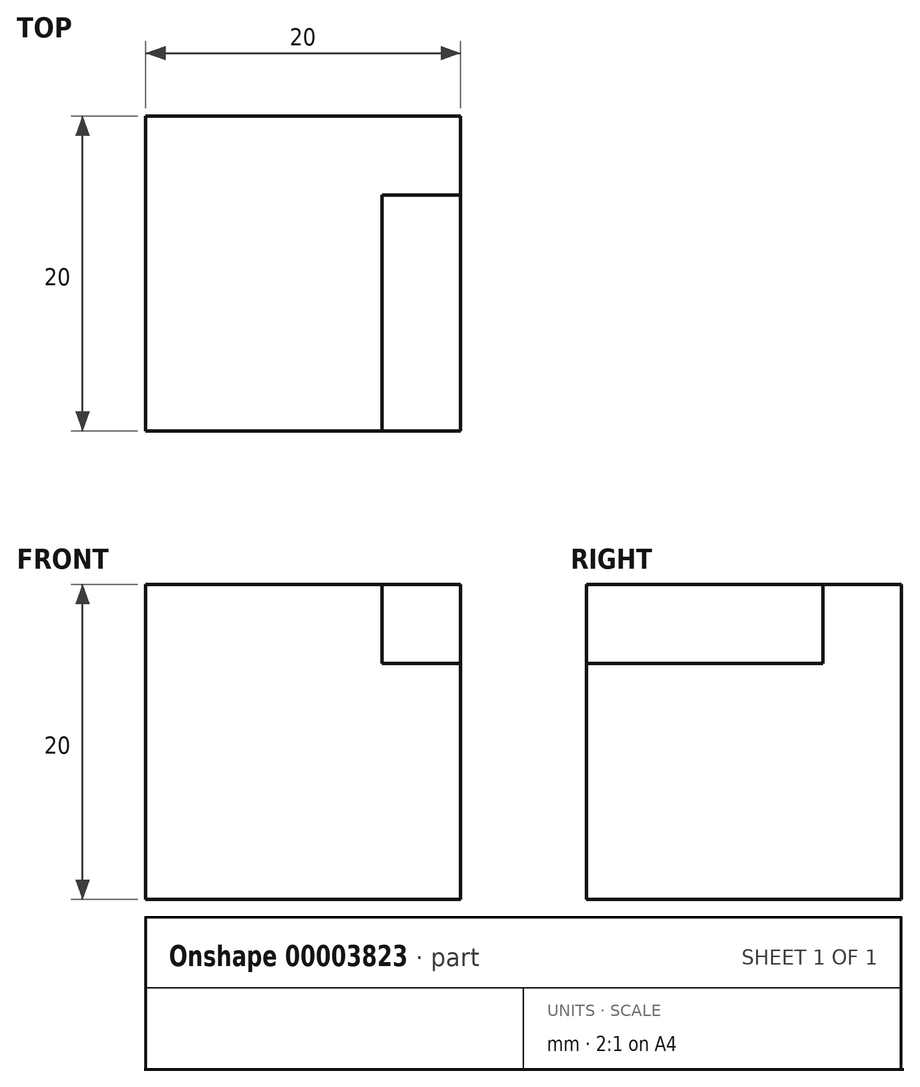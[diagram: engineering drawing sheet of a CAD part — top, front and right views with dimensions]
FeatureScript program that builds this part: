
annotation { "Feature Type Name" : "Feature", "Feature Type Description" : "" }
export const myFeature = defineFeature(function(context is Context, id is Id, definition is map)
    precondition{}
    {
        {
            var Q0;
            Q0=qCreatedBy(makeId("Front.planeOp"),FACE);
            var sketch = newSketch(context, id + "F0", { "sketchPlane" : qUnion([Q0])});
            skLineSegment(sketch, "E0.rect.bottom", {"start": v(10, 10) * mm, "end": v(-10, 10) * mm});
            skLineSegment(sketch, "E0.rect.top", {"start": v(10, -10) * mm, "end": v(-10, -10) * mm});
            skLineSegment(sketch, "E0.rect.left", {"start": v(10, 10) * mm, "end": v(10, -10) * mm});
            skLineSegment(sketch, "E0.rect.right", {"start": v(-10, 10) * mm, "end": v(-10, -10) * mm});
            skPoint(sketch, "E0.rect.middle", {"position": v(0, 0) * mm});
            skSolve(sketch);
        }
        {
            var Q0;
            Q0 = qSketchRegion(id + "F0", true);
            extrude(context, id + "F1", {"entities" : qUnion([Q0]), "endBound" : BoundingType.SYMMETRIC, "depth" : 20 * mm});
        }
        {
            var Q0;
            Q0=makeQuery(id+"F1.opExtrude","CAP_FACE",FACE,{"disambiguationData":[OSD([sQuery(id+"F0.wireOp",EDGE,"E0.rect.bottom"),sQuery(id+"F0.wireOp",EDGE,"E0.rect.top"),sQuery(id+"F0.wireOp",EDGE,"E0.rect.left"),sQuery(id+"F0.wireOp",EDGE,"E0.rect.right")])],"isStart":false});
            var sketch = newSketch(context, id + "F2", { "sketchPlane" : qUnion([Q0])});
            skLineSegment(sketch, "E1.bottom", {"start": v(10, 10) * mm, "end": v(5, 10) * mm});
            skLineSegment(sketch, "E1.top", {"start": v(10, 5) * mm, "end": v(5, 5) * mm});
            skLineSegment(sketch, "E1.left", {"start": v(10, 10) * mm, "end": v(10, 5) * mm});
            skLineSegment(sketch, "E1.right", {"start": v(5, 10) * mm, "end": v(5, 5) * mm});
            skSolve(sketch);
        }
        {
            var Q0;
            Q0 = qSketchRegion(id + "F2", true);
            extrude(context, id + "F3", {"entities" : qUnion([Q0]), "operationType" : NewBodyOperationType.REMOVE, "oppositeDirection" : true, "depth" : 15 * mm});
        }
    });
